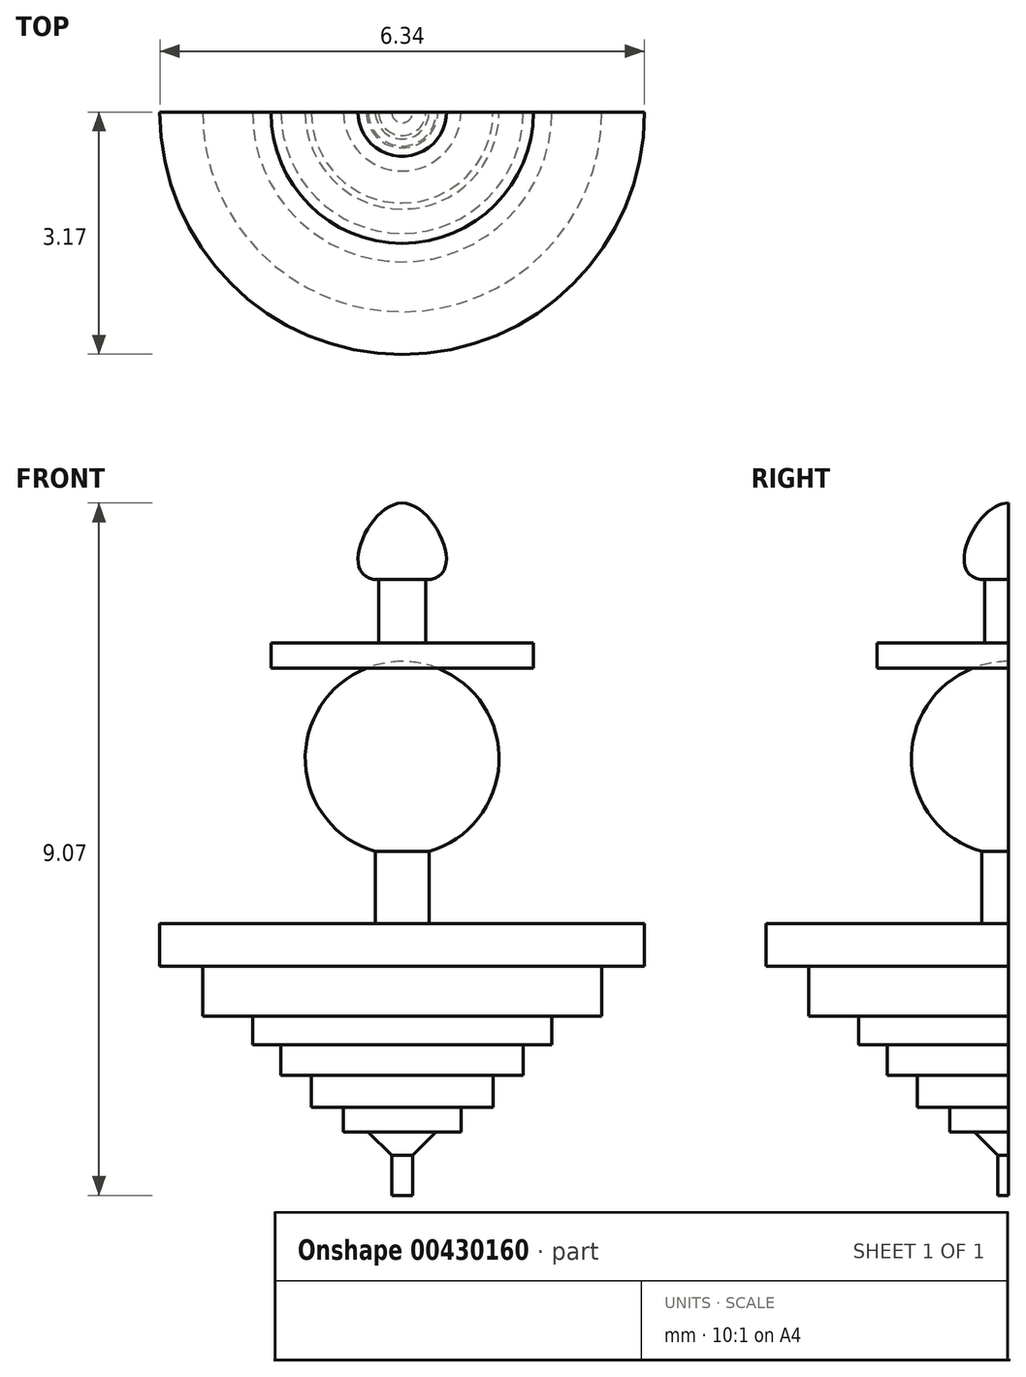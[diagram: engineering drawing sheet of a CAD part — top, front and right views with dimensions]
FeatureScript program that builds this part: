
annotation { "Feature Type Name" : "Feature", "Feature Type Description" : "" }
export const myFeature = defineFeature(function(context is Context, id is Id, definition is map)
    precondition{}
    {
        {
            var Q0;
            Q0=qCreatedBy(makeId("Front.planeOp"),FACE);
            var sketch = newSketch(context, id + "F0", { "sketchPlane" : qUnion([Q0])});
            skPoint(sketch, "E0", {"position": v(-3.18, -5.05) * mm});
            skLineSegment(sketch, "E1", {"start": v(-3.17, -5.05) * mm, "end": v(3.17, -5.05) * mm});
            skPoint(sketch, "E2", {"position": v(0, -5.05) * mm});
            skLineSegment(sketch, "E3.bottom", {"start": v(-3.17, -5.05) * mm, "end": v(3.14, -5.05) * mm});
            skLineSegment(sketch, "E3.top", {"start": v(-3.17, -5.61) * mm, "end": v(3.14, -5.61) * mm});
            skLineSegment(sketch, "E3.left", {"start": v(-3.17, -5.05) * mm, "end": v(-3.17, -5.61) * mm});
            skLineSegment(sketch, "E3.right", {"start": v(3.14, -5.05) * mm, "end": v(3.14, -5.61) * mm});
            skPoint(sketch, "E4.firstSnap0", {"position": v(-0.02, -5.61) * mm});
            skLineSegment(sketch, "E4.bottom", {"start": v(-2.62, -5.61) * mm, "end": v(2.62, -5.61) * mm});
            skLineSegment(sketch, "E4.top", {"start": v(-2.62, -6.27) * mm, "end": v(2.62, -6.27) * mm});
            skLineSegment(sketch, "E4.left", {"start": v(-2.62, -5.61) * mm, "end": v(-2.62, -6.27) * mm});
            skLineSegment(sketch, "E4.right", {"start": v(2.62, -5.61) * mm, "end": v(2.62, -6.27) * mm});
            skPoint(sketch, "E5.oppositeSnap0", {"position": v(-1.59, -6.64) * mm});
            skLineSegment(sketch, "E5.bottom", {"start": v(-1.96, -6.27) * mm, "end": v(1.96, -6.27) * mm});
            skLineSegment(sketch, "E5.top", {"start": v(-1.96, -6.64) * mm, "end": v(1.96, -6.64) * mm});
            skLineSegment(sketch, "E5.left", {"start": v(-1.96, -6.27) * mm, "end": v(-1.96, -6.64) * mm});
            skLineSegment(sketch, "E5.right", {"start": v(1.96, -6.27) * mm, "end": v(1.96, -6.64) * mm});
            skLineSegment(sketch, "E6.bottom", {"start": v(-1.59, -6.64) * mm, "end": v(1.58, -6.64) * mm});
            skLineSegment(sketch, "E6.top", {"start": v(-1.59, -7.04) * mm, "end": v(1.58, -7.04) * mm});
            skLineSegment(sketch, "E6.left", {"start": v(-1.59, -6.64) * mm, "end": v(-1.59, -7.04) * mm});
            skLineSegment(sketch, "E6.right", {"start": v(1.58, -6.64) * mm, "end": v(1.58, -7.04) * mm});
            skLineSegment(sketch, "E7.bottom", {"start": v(-1.2, -7.04) * mm, "end": v(1.2, -7.04) * mm});
            skLineSegment(sketch, "E7.top", {"start": v(-1.2, -7.46) * mm, "end": v(1.2, -7.46) * mm});
            skLineSegment(sketch, "E7.left", {"start": v(-1.2, -7.04) * mm, "end": v(-1.2, -7.46) * mm});
            skLineSegment(sketch, "E7.right", {"start": v(1.2, -7.04) * mm, "end": v(1.2, -7.46) * mm});
            skLineSegment(sketch, "E8.bottom", {"start": v(-0.77, -7.46) * mm, "end": v(0.77, -7.46) * mm});
            skLineSegment(sketch, "E8.top", {"start": v(-0.77, -7.78) * mm, "end": v(0.77, -7.78) * mm});
            skLineSegment(sketch, "E8.left", {"start": v(-0.77, -7.46) * mm, "end": v(-0.77, -7.78) * mm});
            skLineSegment(sketch, "E8.right", {"start": v(0.77, -7.46) * mm, "end": v(0.77, -7.78) * mm});
            skLineSegment(sketch, "E9", {"start": v(0, -8.23) * mm, "end": v(-0.44, -7.78) * mm});
            skLineSegment(sketch, "E10", {"start": v(0, -8.23) * mm, "end": v(0.44, -7.78) * mm});
            skLineSegment(sketch, "E11", {"start": v(0, -5.05) * mm, "end": v(0, -8.23) * mm});
            skLineSegment(sketch, "E12.top", {"start": v(-0.14, -8.6) * mm, "end": v(0.14, -8.6) * mm});
            skLineSegment(sketch, "E12.left", {"start": v(-0.14, -8.09) * mm, "end": v(-0.14, -8.6) * mm});
            skLineSegment(sketch, "E12.right", {"start": v(0.14, -8.09) * mm, "end": v(0.14, -8.6) * mm});
            skLineSegment(sketch, "E13", {"start": v(0, -8.23) * mm, "end": v(0, -8.6) * mm});
            skLineSegment(sketch, "E14.bottom", {"start": v(-0.35, -4.1) * mm, "end": v(0.35, -4.1) * mm});
            skLineSegment(sketch, "E14.top", {"start": v(-0.35, -5.05) * mm, "end": v(0.35, -5.05) * mm});
            skLineSegment(sketch, "E14.left", {"start": v(-0.35, -4.1) * mm, "end": v(-0.35, -5.05) * mm});
            skLineSegment(sketch, "E14.right", {"start": v(0.35, -4.1) * mm, "end": v(0.35, -5.05) * mm});
            skLineSegment(sketch, "E15", {"start": v(0, -4.1) * mm, "end": v(0, -5.05) * mm});
            skCircle(sketch, "E16", {"center": v(0, -2.89) * mm, "radius": 1.27 * mm});
            skLineSegment(sketch, "E17.bottom", {"start": v(-1.72, -1.38) * mm, "end": v(1.72, -1.38) * mm});
            skLineSegment(sketch, "E17.top", {"start": v(-1.72, -1.7) * mm, "end": v(1.72, -1.7) * mm});
            skLineSegment(sketch, "E17.left", {"start": v(-1.72, -1.38) * mm, "end": v(-1.72, -1.7) * mm});
            skLineSegment(sketch, "E17.right", {"start": v(1.72, -1.38) * mm, "end": v(1.72, -1.7) * mm});
            skLineSegment(sketch, "E18.bottom", {"start": v(-0.3, -0.54) * mm, "end": v(0.3, -0.54) * mm});
            skLineSegment(sketch, "E18.top", {"start": v(-0.3, -1.38) * mm, "end": v(0.3, -1.38) * mm});
            skLineSegment(sketch, "E18.left", {"start": v(-0.3, -0.54) * mm, "end": v(-0.3, -1.38) * mm});
            skLineSegment(sketch, "E18.right", {"start": v(0.3, -0.54) * mm, "end": v(0.3, -1.38) * mm});
            skPoint(sketch, "E19", {"position": v(0, -1.38) * mm});
            skPoint(sketch, "E20", {"position": v(0, -0.54) * mm});
            skPoint(sketch, "E21", {"position": v(0, -1.7) * mm});
            skPoint(sketch, "E22", {"position": v(0, -4.16) * mm});
            skPoint(sketch, "E23", {"position": v(0, -1.62) * mm});
            skLineSegment(sketch, "E24", {"start": v(0, -1.62) * mm, "end": v(0, -4.16) * mm});
            skLineSegment(sketch, "E25", {"start": v(0, -1.7) * mm, "end": v(0, -1.38) * mm});
            skLineSegment(sketch, "E26", {"start": v(0, -1.38) * mm, "end": v(0, -0.54) * mm});
            skPoint(sketch, "E27", {"position": v(0, 0.46) * mm});
            skFitSpline(sketch, "E28", {"points": [v(-0.3, -0.54) * mm, v(0, 0.46) * mm, v(0.3, -0.54) * mm], "startDerivative": vector(-3.43, -0.01) * mm, "endDerivative": vector(-3.37, -0.03) * mm});
            skLineSegment(sketch, "E29", {"start": v(0, 0.46) * mm, "end": v(0, -0.54) * mm});
            skSolve(sketch);
        }
        {
            var Q0;
            {var subQ5=sQuery(id+"F0.wireOp",EDGE,"E3.left");Q0=makeQuery(id+"F0.imprint","IMPRINT",FACE,{"disambiguationData":[TD([[makeQuery(id+"F0.imprint","IMPRINT",EDGE,{"derivedFrom":subQ5}),1.0]])]});}
            var Q1;
            {var subQ5=sQuery(id+"F0.wireOp",EDGE,"E4.left");Q1=makeQuery(id+"F0.imprint","IMPRINT",FACE,{"disambiguationData":[TD([[makeQuery(id+"F0.imprint","IMPRINT",EDGE,{"derivedFrom":subQ5}),1.0]])]});}
            var Q2;
            {var subQ5=sQuery(id+"F0.wireOp",EDGE,"E5.left");Q2=makeQuery(id+"F0.imprint","IMPRINT",FACE,{"disambiguationData":[TD([[makeQuery(id+"F0.imprint","IMPRINT",EDGE,{"derivedFrom":subQ5}),1.0]])]});}
            var Q3;
            {var subQ5=sQuery(id+"F0.wireOp",EDGE,"E6.left");Q3=makeQuery(id+"F0.imprint","IMPRINT",FACE,{"disambiguationData":[TD([[makeQuery(id+"F0.imprint","IMPRINT",EDGE,{"derivedFrom":subQ5}),1.0]])]});}
            var Q4;
            {var subQ5=sQuery(id+"F0.wireOp",EDGE,"E7.left");Q4=makeQuery(id+"F0.imprint","IMPRINT",FACE,{"disambiguationData":[TD([[makeQuery(id+"F0.imprint","IMPRINT",EDGE,{"derivedFrom":subQ5}),1.0]])]});}
            var Q5;
            {var subQ0=sQuery(id+"F0.wireOp",EDGE,"E8.left");Q5=makeQuery(id+"F0.imprint","IMPRINT",FACE,{"disambiguationData":[TD([[makeQuery(id+"F0.imprint","IMPRINT",EDGE,{"derivedFrom":subQ0}),1.0]])]});}
            var Q6;
            {var subQ0=sQuery(id+"F0.wireOp",EDGE,"E9");var subQ1=sQuery(id+"F0.wireOp",EDGE,"E8.top");var subQ2=makeQuery(id+"F0.imprint","INTERSECT",VERTEX,{"derivedFrom":[subQ1,subQ0]});Q6=makeQuery(id+"F0.imprint","IMPRINT",FACE,{"disambiguationData":[TD([[makeQuery(id+"F0.imprint","IMPRINT",EDGE,{"disambiguationData":[TD([[subQ2,-1.0]])],"derivedFrom":subQ1}),-1.0]])]});}
            var Q7;
            {var subQ2=sQuery(id+"F0.wireOp",EDGE,"E12.left");Q7=makeQuery(id+"F0.imprint","IMPRINT",FACE,{"disambiguationData":[TD([[makeQuery(id+"F0.imprint","IMPRINT",EDGE,{"derivedFrom":subQ2}),1.0]])]});}
            var Q8;
            {var subQ0=sQuery(id+"F0.wireOp",EDGE,"E15");Q8=makeQuery(id+"F0.imprint","IMPRINT",FACE,{"disambiguationData":[TD([[makeQuery(id+"F0.imprint","IMPRINT",EDGE,{"derivedFrom":subQ0}),-1.0]])]});}
            var Q9;
            Q9=sQuery(id+"F0.wireOp",EDGE,"E11");
            revolve(context, id + "F1", {"entities" : qUnion([Q0, Q1, Q2, Q3, Q4, Q5, Q6, Q7, Q8]), "axis" : qUnion([Q9]), "revolveType" : RevolveType.ONE_DIRECTION, "oppositeDirection" : true, "angle" : 180 * degree});
        }
        {
            var Q0;
            {var subQ5=sQuery(id+"F0.wireOp",EDGE,"E14.bottom");var subQ7=sQuery(id+"F0.wireOp",EDGE,"E14.left");var subQ9=makeQuery(id+"F0.imprint","INTERSECT",VERTEX,{"derivedFrom":[subQ5,subQ7]});Q0=makeQuery(id+"F0.imprint","IMPRINT",FACE,{"disambiguationData":[TD([[makeQuery(id+"F0.imprint","IMPRINT",EDGE,{"disambiguationData":[TD([[subQ9,-1.0]])],"derivedFrom":subQ5}),1.0]])]});}
            var Q1;
            Q1=sQuery(id+"F0.wireOp",EDGE,"E24");
            revolve(context, id + "F2", {"entities" : qUnion([Q0]), "axis" : qUnion([Q1]), "revolveType" : RevolveType.ONE_DIRECTION, "oppositeDirection" : true, "angle" : 180 * degree});
        }
        {
            var Q0;
            {var subQ0=sQuery(id+"F0.wireOp",EDGE,"E17.left");Q0=makeQuery(id+"F0.imprint","IMPRINT",FACE,{"disambiguationData":[TD([[makeQuery(id+"F0.imprint","IMPRINT",EDGE,{"derivedFrom":subQ0}),1.0]])]});}
            var Q1;
            Q1=sQuery(id+"F0.wireOp",EDGE,"E25");
            revolve(context, id + "F3", {"entities" : qUnion([Q0]), "axis" : qUnion([Q1]), "revolveType" : RevolveType.ONE_DIRECTION, "angle" : 180 * degree});
        }
        {
            var Q0;
            {var subQ0=sQuery(id+"F0.wireOp",EDGE,"E18.left");Q0=makeQuery(id+"F0.imprint","IMPRINT",FACE,{"disambiguationData":[TD([[makeQuery(id+"F0.imprint","IMPRINT",EDGE,{"derivedFrom":subQ0}),1.0]])]});}
            var Q1;
            Q1=sQuery(id+"F0.wireOp",EDGE,"E26");
            revolve(context, id + "F4", {"operationType" : NewBodyOperationType.ADD, "entities" : qUnion([Q0]), "axis" : qUnion([Q1]), "revolveType" : RevolveType.ONE_DIRECTION, "angle" : 180 * degree});
        }
        {
            var Q0;
            {var subQ3=sQuery(id+"F0.wireOp",EDGE,"E29");Q0=makeQuery(id+"F0.imprint","IMPRINT",FACE,{"disambiguationData":[TD([[makeQuery(id+"F0.imprint","IMPRINT",EDGE,{"derivedFrom":subQ3}),-1.0]])]});}
            var Q1;
            Q1=sQuery(id+"F0.wireOp",EDGE,"E29");
            revolve(context, id + "F5", {"entities" : qUnion([Q0]), "axis" : qUnion([Q1]), "revolveType" : RevolveType.ONE_DIRECTION, "oppositeDirection" : true, "angle" : 180 * degree});
        }
    });
